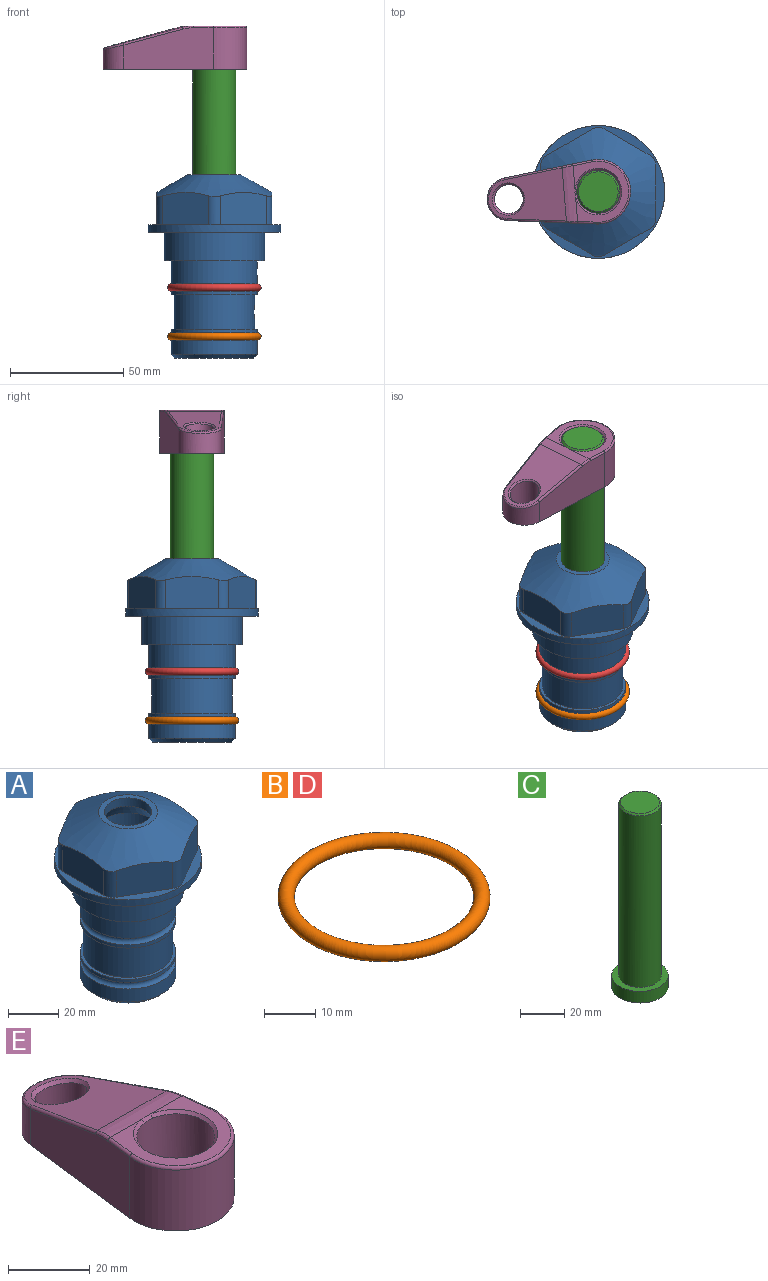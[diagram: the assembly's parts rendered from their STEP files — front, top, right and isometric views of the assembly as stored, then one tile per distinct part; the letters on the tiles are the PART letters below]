
ASSEMBLY  parts=5 mates=4
PART A: 36 faces, bbox 58.7x58.7x81 mm
  f0: cylinder r=17.78mm len=35.56mm, axis (0,0,1), area 1670.8mm2, adj f23,f24,f31
  f1: cylinder r=19.05mm len=38.1mm, axis (0,0,1), area 1191.9mm2, adj f26,f27,f30
  f2: plane 58.66x58.66mm, normal (0,0,-1), area 1150.6mm2, adj f3,f28
  f3: cylinder r=29.33mm len=58.66mm, axis (0,0,-1), area 585.1mm2, adj f2,f4
  f4: plane 58.66x58.66mm, normal (0,0,1), area 475.9mm2, adj f3,f5,f6,f7,f8,f9,f10,f11
  f5: plane 20.32x14.34mm, normal (-0.5,0.87,0), area 324.4mm2, adj f4,f15,f16,f17
  f6: plane 20.32x14.34mm, normal (0.5,0.87,0), area 324.4mm2, adj f4,f14,f15,f17
  f7: plane 23.48x14.34mm, normal (1,0,0), area 324.4mm2, adj f4,f13,f14,f17
  f8: plane 20.32x14.34mm, normal (0.5,-0.87,0), area 324.4mm2, adj f4,f12,f13,f17
  f9: plane 20.32x14.34mm, normal (-0.5,-0.87,0), area 324.4mm2, adj f4,f11,f12,f17
  f10: plane 23.48x14.34mm, normal (-1,0,0), area 324.4mm2, adj f4,f11,f16,f17
  f11: cylinder r=5.08mm len=12.85mm, axis (0,0,-1), area 67.2mm2, adj f4,f9,f10,f17
  f12: cylinder r=5.08mm len=12.85mm, axis (0,0,-1), area 67.2mm2, adj f4,f8,f9,f17
  f13: cylinder r=5.08mm len=12.85mm, axis (0,0,-1), area 67.2mm2, adj f4,f7,f8,f17
  f14: cylinder r=5.08mm len=12.85mm, axis (0,0,-1), area 67.2mm2, adj f4,f6,f7,f17
  f15: cylinder r=5.08mm len=12.85mm, axis (0,0,-1), area 67.2mm2, adj f4,f5,f6,f17
  f16: cylinder r=5.08mm len=12.85mm, axis (0,0,-1), area 67.2mm2, adj f4,f5,f10,f17
  f17: cone r=11.73mm half-angle=60deg, axis (0,0,-1), area 2071.8mm2, adj f5,f6,f7,f8,f9,f10,f11,f12
  f18: plane 23.46x23.46mm, normal (0,0,1), area 147.4mm2, adj f17,f35
  f19: plane 34.93x34.93mm, normal (0,0,-1), area 958mm2, adj f29
  f20: cylinder r=19.05mm len=38.1mm, axis (0,0,1), area 760.1mm2, adj f21,f29
  f21: torus R=19.05mm, axis (0,0,1), area 565.3mm2, adj f20,f22
  f22: cylinder r=19.05mm len=38.1mm, axis (0,0,1), area 190mm2, adj f21,f23
  f23: plane 38.1x38.1mm, normal (0,0,1), area 146.9mm2, adj f0,f22
  f24: plane 38.1x38.1mm, normal (0,0,-1), area 146.9mm2, adj f0,f25
  f25: cylinder r=19.05mm len=38.1mm, axis (0,0,1), area 190mm2, adj f24,f26
  f26: torus R=19.05mm, axis (0,0,1), area 565.3mm2, adj f1,f25
  f27: plane 44.45x44.45mm, normal (0,0,-1), area 411.7mm2, adj f1,f28
  f28: cylinder r=22.23mm len=44.45mm, axis (0,0,1), area 1773.5mm2, adj f2,f27
  f29: cone r=19.05mm half-angle=45deg, axis (0,0,1), area 257.5mm2, adj f19,f20
  f30: cylinder r=3.17mm len=6.75mm, axis (-1,0,0), area 128mm2, adj f1,f33
  f31: cylinder r=3.17mm len=6.35mm, axis (-1,0,0), area 102.5mm2, adj f0,f33
  f32: plane 25.4x25.4mm, normal (0,0,1), area 506.7mm2, adj f33
  f33: cylinder r=12.7mm len=66.42mm, axis (0,0,-1), area 5236.2mm2, adj f30,f31,f32,f34
  f34: cone r=9.53mm half-angle=30deg, axis (0,0,-1), area 443.4mm2, adj f33,f35
  f35: cylinder r=9.53mm len=19.05mm, axis (0,0,-1), area 240.9mm2, adj f18,f34
PART B: 1 faces, bbox 44.7x44.7x3.2 mm
  f0: torus R=19.05mm, axis (0,0,1), area 1193.9mm2
PART C: 6 faces, bbox 25.4x25.4x101.6 mm
  f0: plane 17.46x17.46mm, normal (0,0,1), area 239.5mm2, adj f5
  f1: plane 25.4x25.4mm, normal (0,0,-1), area 506.7mm2, adj f2
  f2: cylinder r=12.7mm len=25.4mm, axis (0,0,1), area 506.7mm2, adj f1,f3
  f3: plane 25.4x25.4mm, normal (0,0,1), area 221.7mm2, adj f2,f4
  f4: cylinder r=9.53mm len=94.46mm, axis (0,0,1), area 5653mm2, adj f3,f5
  f5: cone r=8.73mm half-angle=45deg, axis (0,0,-1), area 64.4mm2, adj f0,f4
PART D: same geometry as B
PART E: 31 faces, bbox 31.7x65.5x19.8 mm
  f0: plane 39.12x18.26mm, normal (0.99,0.12,0), area 612.2mm2, adj f1,f4,f7,f11,f13,f15
  f1: cylinder r=9.53mm len=18.91mm, axis (0,0,-1), area 296.1mm2, adj f0,f2,f7,f17
  f2: plane 39.12x18.26mm, normal (-0.99,0.12,0), area 612.2mm2, adj f1,f4,f7,f12,f14,f16
  f3: cylinder r=6.35mm len=12.7mm, axis (0,0,-1), area 362.4mm2, adj f7,f18
  f4: cylinder r=14.29mm len=28.58mm, axis (0,0,-1), area 882.2mm2, adj f0,f2,f7,f10
  f5: cylinder r=9.53mm len=19.05mm, axis (0,0,-1), area 1092.6mm2, adj f7,f19,f20
  f6: plane 26.99x23.69mm, normal (0,0,1), area 216.2mm2, adj f9,f10,f11,f12,f19
  f7: plane 63.5x28.58mm, normal (0,0,-1), area 661.8mm2, adj f0,f1,f2,f3,f4,f5,f22,f23
  f8: plane 33.52x23.6mm, normal (0,0.26,0.97), area 486mm2, adj f9,f15,f16,f17,f18
  f9: cylinder r=19.05mm len=24.72mm, axis (1,0,0), area 120.4mm2, adj f6,f8,f13,f14,f20
  f10: torus R=13.49mm, axis (0,0,1), area 59mm2, adj f4,f6,f11,f12
  f11: cylinder r=0.79mm len=8.67mm, axis (0.12,-0.99,0), area 10.8mm2, adj f0,f6,f10,f13
  f12: cylinder r=0.79mm len=8.67mm, axis (0.12,0.99,0), area 10.8mm2, adj f2,f6,f10,f14
  f13: bspline ~4.95x1.42mm, area 6.1mm2, adj f0,f9,f11,f15
  f14: bspline ~4.95x1.42mm, area 6.1mm2, adj f2,f9,f12,f16
  f15: cylinder r=0.79mm len=25.95mm, axis (0.12,-0.96,0.26), area 32.9mm2, adj f0,f8,f13,f17
  f16: cylinder r=0.79mm len=25.95mm, axis (0.12,0.96,-0.26), area 32.9mm2, adj f2,f8,f14,f17
  f17: bspline ~18.91x8.38mm, area 30mm2, adj f1,f8,f15,f16
  f18: bspline ~14.29x14.29mm, area 48.3mm2, adj f3,f8
  f19: cone r=9.53mm half-angle=45deg, axis (0,0,1), area 66.5mm2, adj f5,f6,f20
  f20: bspline ~3.22x0.96mm, area 3.5mm2, adj f5,f9,f19
  f21: plane 2.75x2.72mm, normal (0,0,-1), area 2.9mm2, adj f23,f25,f28
  f22: plane 23.05x15.88mm, normal (-0.99,-0.12,0), area 323.6mm2, adj f7,f25,f26,f27,f28,f29
  f23: plane 23.05x15.88mm, normal (0.99,-0.12,0), area 323.6mm2, adj f7,f21,f25,f27,f28,f30
  f24: cylinder r=9.53mm len=10.69mm, axis (0,0,-1), area 114.7mm2, adj f7,f27,f29,f30
  f25: cylinder r=12.7mm len=20.59mm, axis (0,0,-1), area 381.1mm2, adj f7,f21,f22,f23,f26,f28
  f26: plane 2.75x2.72mm, normal (0,0,-1), area 2.9mm2, adj f22,f25,f28
  f27: plane 19.72x18.37mm, normal (0,-0.26,-0.97), area 291.8mm2, adj f22,f23,f24,f28,f29,f30
  f28: cylinder r=15.88mm len=19.92mm, axis (1,0,0), area 54.8mm2, adj f21,f22,f23,f25,f26,f27
  f29: cylinder r=1.59mm len=11mm, axis (0,0,-1), area 34.7mm2, adj f7,f22,f24,f27
  f30: cylinder r=1.59mm len=11mm, axis (0,0,-1), area 34.7mm2, adj f7,f23,f24,f27
PLACE A at identity fixed
PLACE B t=(0,0,-21.59)mm
PLACE C rot(axis=(0,0,1),94.7deg) t=(0,0,27.55)mm
PLACE D at identity
PLACE E rot(axis=(0,0,1),94.7deg) t=(0,0,27.55)mm
MATE fastened E.f4 <-> C.f2  axis (0,0,1) through (0,0,91.05)mm
MATE fastened D.f0 <-> A.f0  axis (0,0,1) through (0,0,-24.51)mm
MATE cylindrical A.f0 <-> C.f2  axis (0,0,1) through (0,0,-50.55)mm
MATE fastened B.f0 <-> A.f0  axis (0,0,1) through (0,0,-46.1)mm
